# Revit family: KARO-L-3500-8xx-Fx
name_source: partatom
category: Oprawy oświetleniowe
units: mm (PartAtom-declared; Revit-internal decimal feet)

## family parameters
Numer OmniClass = 23.80.70.11
Obiekt nadrzędny = Powierzchnia
Punkt obliczania pomieszczeń = Nie
Tnij formami wycięć po wczytaniu = Nie
Typ części = Normalny
Tytuł OmniClass = Luminaries for Internal Lighting
Współdzielony = Nie
Wymiar okrągłego złącza = Użyj średnicy
Źródło światła = Tak

## types (4) — shared parameters
Emituj kształt widoczny w renderingu = Nie
Emituj z długości prostokąta = 105 mm  [stored 0.344488 ft]
Emituj z szerokości prostokąta = 105 mm  [stored 0.344488 ft]
Filtr koloru = 16777215
Kod zespołu = D5020200
Lampa = LED
Obciążenie pozorne = 37 VA
Odchylenie kierunku = 90.00°
Plik sieci fotometrycznej = KARO-S 2500-840 F.IES
Producent = RIDI Leuchten GmbH
URL = www.ridi.de
Zmiana temperatury barwowej przyciemniania lampy = <Brak>
brand = RIDI
conformity mark = CE
electrical safety class = 1
height = 249 mm  [stored 0.816929 ft]
ingress protection (IP) code = IP20
length = 177 mm  [stored 0.580709 ft]
nominal frequency = 50-60Hz
nominal voltage = 230
rated input power = 37
voltage type (AC, DC, UC) = AC
weight = 2,3 kg
width = 130 mm  [stored 0.426509 ft]
zero-valued in all types: Domyślna rzędna

## per-type parameters (varying)
| type | Model | product name |
| KARO-L 3500-830 F | 0321896 | KARO-L 3500-830 F |
| KARO-L 3500-830-F-DA | 0331896 | KARO-L 3500-830 F-DA |
| KARO-L 3500-840 F | 0321889 | KARO-L 3500-840 F |
| KARO-L 3500-840 F-DA | 0331889 | KARO-L 3500-840 F-DA |

note: [stored X ft] marks values corroborated as IEEE doubles in the binary element streams (Revit-internal decimal feet)
